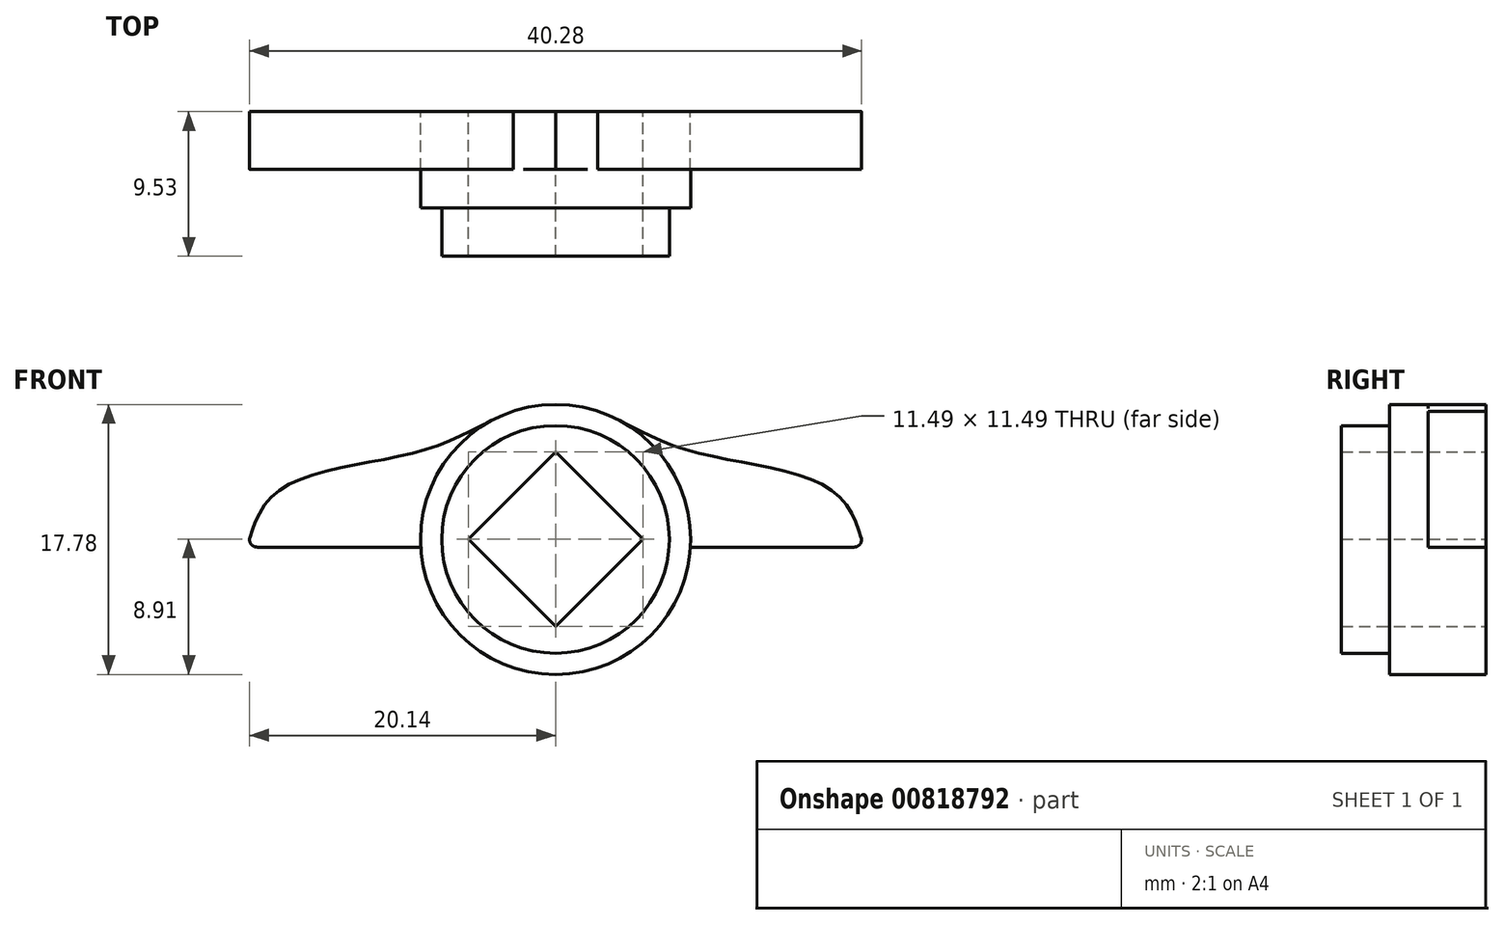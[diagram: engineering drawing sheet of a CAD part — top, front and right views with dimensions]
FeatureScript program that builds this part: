
annotation { "Feature Type Name" : "Feature", "Feature Type Description" : "" }
export const myFeature = defineFeature(function(context is Context, id is Id, definition is map)
    precondition{}
    {
        {
            var Q0;
            Q0=qCreatedBy(makeId("Front.planeOp"),FACE);
            var sketch = newSketch(context, id + "F0", { "sketchPlane" : qUnion([Q0])});
            skLineSegment(sketch, "E0", {"start": v(0, -6.55) * mm, "end": v(0, 6.2) * mm, "construction": true});
            skCircle(sketch, "E1", {"center": v(0, 0) * mm, "radius": 8.9 * mm});
            skLineSegment(sketch, "E2", {"start": v(0, -0.5) * mm, "end": v(20.32, -0.5) * mm});
            skLineSegment(sketch, "E3", {"start": v(-1.88, 0) * mm, "end": v(2.04, 0) * mm, "construction": true});
            skFitSpline(sketch, "E4", {"points": [v(0, 8.9) * mm, v(2.78, 8.45) * mm, v(8.6, 5.9) * mm, v(18.43, 3.04) * mm, v(20.32, -0.5) * mm], "startDerivative": vector(12.38, -0.7) * mm, "endDerivative": vector(3.8, -11) * mm});
            skLineSegment(sketch, "E5.bottom", {"start": v(0, 5.77) * mm, "end": v(-5.75, 0.02) * mm});
            skLineSegment(sketch, "E5.top", {"start": v(5.75, 0.02) * mm, "end": v(0, -5.73) * mm});
            skLineSegment(sketch, "E5.left", {"start": v(0, 5.77) * mm, "end": v(5.75, 0.02) * mm});
            skLineSegment(sketch, "E5.right", {"start": v(-5.75, 0.02) * mm, "end": v(0, -5.73) * mm});
            skFitSpline(sketch, "E6.MirrorCS", {"points": [v(0, 8.9) * mm, v(-2.78, 8.45) * mm, v(-8.6, 5.9) * mm, v(-18.43, 3.04) * mm, v(-20.32, -0.5) * mm], "startDerivative": vector(-12.38, -0.7) * mm, "endDerivative": vector(-3.8, -11) * mm});
            skLineSegment(sketch, "E7.MirrorCS", {"start": v(0, -0.5) * mm, "end": v(-20.32, -0.5) * mm});
            skSolve(sketch);
        }
        {
            var Q0;
            {var subQ12=sQuery(id+"F0.wireOp",EDGE,"E5.bottom");Q0=makeQuery(id+"F0.imprint","IMPRINT",FACE,{"disambiguationData":[TD([[makeQuery(id+"F0.imprint","IMPRINT",EDGE,{"derivedFrom":subQ12}),-1.0]])]});}
            var Q1;
            {var subQ0=sQuery(id+"F0.wireOp",EDGE,"E6.MirrorCS");var subQ1=sQuery(id+"F0.wireOp",EDGE,"E1");var subQ2=makeQuery(id+"F0.imprint","INTERSECT",VERTEX,{"disambiguationData":[OD(2.0)],"derivedFrom":[subQ1,subQ0]});Q1=makeQuery(id+"F0.imprint","IMPRINT",FACE,{"disambiguationData":[TD([[makeQuery(id+"F0.imprint","IMPRINT",EDGE,{"disambiguationData":[TD([[subQ2,-1.0]])],"derivedFrom":subQ1}),-1.0]])]});}
            var Q2;
            {var subQ0=sQuery(id+"F0.wireOp",EDGE,"E4");var subQ1=sQuery(id+"F0.wireOp",EDGE,"E1");var subQ2=makeQuery(id+"F0.imprint","INTERSECT",VERTEX,{"disambiguationData":[OD(0.0)],"derivedFrom":[subQ1,subQ0]});Q2=makeQuery(id+"F0.imprint","IMPRINT",FACE,{"disambiguationData":[TD([[makeQuery(id+"F0.imprint","IMPRINT",EDGE,{"disambiguationData":[TD([[subQ2,1.0]])],"derivedFrom":subQ1}),-1.0]])]});}
            var Q3;
            {var subQ5=sQuery(id+"F0.wireOp",EDGE,"E2");var subQ6=sQuery(id+"F0.wireOp",EDGE,"E1");var subQ7=makeQuery(id+"F0.imprint","INTERSECT",VERTEX,{"derivedFrom":[subQ6,subQ5]});Q3=makeQuery(id+"F0.imprint","IMPRINT",FACE,{"disambiguationData":[TD([[makeQuery(id+"F0.imprint","IMPRINT",EDGE,{"disambiguationData":[TD([[subQ7,1.0]])],"derivedFrom":subQ6}),1.0]])]});}
            extrude(context, id + "F1", {"entities" : qUnion([Q0, Q1, Q2, Q3]), "depth" : 3.8 * mm, "offsetDistance" : 25.4 * mm});
        }
        {
            var Q0;
            Q0=makeQuery(id+"F1.opExtrude","CAP_FACE",FACE,{"disambiguationData":[OSD([sQuery(id+"F0.wireOp",EDGE,"E1"),sQuery(id+"F0.wireOp",EDGE,"E2"),sQuery(id+"F0.wireOp",EDGE,"E4"),sQuery(id+"F0.wireOp",EDGE,"E5.bottom"),sQuery(id+"F0.wireOp",EDGE,"E5.top"),sQuery(id+"F0.wireOp",EDGE,"E5.left"),sQuery(id+"F0.wireOp",EDGE,"E5.right"),sQuery(id+"F0.wireOp",EDGE,"E6.MirrorCS"),sQuery(id+"F0.wireOp",EDGE,"E7.MirrorCS")])],"isStart":false});
            var sketch = newSketch(context, id + "F2", { "sketchPlane" : qUnion([Q0])});
            skCircle(sketch, "E8.0", {"center": v(0, 0) * mm, "radius": 8.9 * mm});
            skLineSegment(sketch, "E8.1", {"start": v(0, 5.77) * mm, "end": v(-5.75, 0.02) * mm});
            skLineSegment(sketch, "E8.2", {"start": v(0, 5.77) * mm, "end": v(5.75, 0.02) * mm});
            skLineSegment(sketch, "E8.3", {"start": v(-5.75, 0.02) * mm, "end": v(0, -5.73) * mm});
            skLineSegment(sketch, "E8.4", {"start": v(5.75, 0.02) * mm, "end": v(0, -5.73) * mm});
            skSolve(sketch);
        }
        {
            var Q0;
            Q0 = qSketchRegion(id + "F2", true);
            extrude(context, id + "F3", {"entities" : qUnion([Q0]), "operationType" : NewBodyOperationType.ADD, "depth" : 2.54 * mm, "offsetDistance" : 25.4 * mm});
        }
        {
            var Q0;
            Q0=makeQuery(id+"F3.opExtrude","CAP_FACE",FACE,{"disambiguationData":[OSD([sQuery(id+"F2.wireOp",EDGE,"E8.0"),sQuery(id+"F2.wireOp",EDGE,"E8.1"),sQuery(id+"F2.wireOp",EDGE,"E8.2"),sQuery(id+"F2.wireOp",EDGE,"E8.3"),sQuery(id+"F2.wireOp",EDGE,"E8.4")])],"isStart":false});
            var sketch = newSketch(context, id + "F4", { "sketchPlane" : qUnion([Q0])});
            skLineSegment(sketch, "E9.0", {"start": v(-5.75, 0.02) * mm, "end": v(0, -5.73) * mm});
            skLineSegment(sketch, "E9.1", {"start": v(5.75, 0.02) * mm, "end": v(0, -5.73) * mm});
            skLineSegment(sketch, "E9.2", {"start": v(0, 5.77) * mm, "end": v(5.75, 0.02) * mm});
            skLineSegment(sketch, "E9.3", {"start": v(0, 5.77) * mm, "end": v(-5.75, 0.02) * mm});
            skPoint(sketch, "E9.4", {"position": v(0, 0) * mm});
            skCircle(sketch, "E10", {"center": v(0, 0) * mm, "radius": 7.5 * mm});
            skSolve(sketch);
        }
        {
            var Q0;
            Q0=makeQuery(id+"F4.imprint","IMPRINT",FACE,{"disambiguationData":[TD([[makeQuery(id+"F4.imprint","IMPRINT",EDGE,{"derivedFrom":sQuery(id+"F4.wireOp",EDGE,"E9.0")}),-1.0]])]});
            extrude(context, id + "F5", {"entities" : qUnion([Q0]), "operationType" : NewBodyOperationType.ADD, "depth" : 3.17 * mm, "offsetDistance" : 25.4 * mm});
        }
        {
            var Q0;
            Q0=makeQuery(id+"F1.opExtrude","SWEPT_EDGE",EDGE,{"disambiguationData":[OSD([sQuery(id+"F0.wireOp",EDGE,"E2"),sQuery(id+"F0.wireOp",EDGE,"E4")])]});
            var Q1;
            Q1=makeQuery(id+"F1.opExtrude","SWEPT_EDGE",EDGE,{"disambiguationData":[OSD([sQuery(id+"F0.wireOp",EDGE,"E6.MirrorCS"),sQuery(id+"F0.wireOp",EDGE,"E7.MirrorCS")])]});
            fillet(context, id + "F6", {"entities" : qUnion([Q0, Q1]), "radius" : 0.5 * mm, "tangentPropagation" : true, "allowEdgeOverflow" : false});
        }
    });
